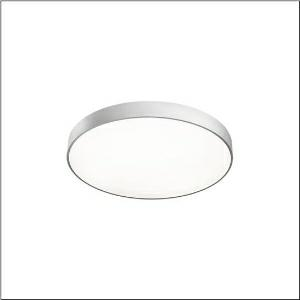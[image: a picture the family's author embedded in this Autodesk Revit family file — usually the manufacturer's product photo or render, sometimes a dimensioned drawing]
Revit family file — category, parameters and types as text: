
# Revit family: round_21_m_51mr36fm8321s
name_source: partatom
category: Lighting Fixtures
units: mm (PartAtom-declared; Revit-internal decimal feet)

## family parameters
Cut with Voids When Loaded = No
Host = Face
Light Source = No
Part Type = Normal
Room Calculation Point = No
Round Connector Dimension = Use Diameter
Shared = No

## types (1)
- --- (1 x LED, 8540 lm, 62.6 W, 3000K)
    Apparent Load = 63 VA
    CIE Flux Codes = 49 80 96 100 100
    Color Rendering = 80
    Color Temperature = 3000K
    Default Elevation = 1800 mm
    Description = Round 21 M, wall and ceiling luminaire, primary optical cover: cover, of PMMA, opal, light emission: direct distribution, primary light characteristic: symmetric, installation type: suspended mounting, surface-mounted, LED, rated luminous flux: 7.700lm, luminous efficacy: 127lm/W, light colour: 830, colour temperature: 3000K, control gear: ON/OFF Multilumen, with terminal, 3-pole, mains connection: 230V, AC, 50/60Hz, rated input power: 61W, housing, of aluminium, coated, silver, diameter: 600mm, height: 62mm, protection rating (complete): IP40, insulation class (complete): insulation class I (protective earthing), certification: CE, impact resistance: IK04, permissible operating ambient temperature: -10..+35°C, packaging unit: 1 piece
    Height = 87 mm
    Lamp = 1 x LED
    Lamp Light Flux = 8540 lm
    Lamp Power = 62.6 W
    Lamp count = 1
    Length = 600 mm
    Luminous efficacy = 136 lm/W
    Manufacturer = Siteco
    ModVariant = No
    Model = 51MR36FM8321S
    Mounting Place = Ceiling
    Mounting Type = Surface mounted
    Number of Poles = 1
    OnlyDefault = Yes
    Power Factor = 1
    Product Name = Round 21 M
    Product group = wall and ceiling luminaire
    ProductGroupID = 304
    Protection Class = Protection class I
    Protection Degree = IP 40
    RLX_Detail_Level = 1
    RLX_Emergency_Light_Flux = 0 lm
    RLX_Emergency_Type = 0
    RLX_Emergency_Type_DB = No
    RlxData = <blob elided: 17473 chars, md5=b82f56c6>
    Socket = socket
    Standby Power = 0 W
    System Light Flux = 8540 lm
    System Power = 63 W
    Type Comments = factory setting: luminous flux: 100 % | (ON | ON | ON | ON) | 700 mA
    Type Image = l_1258303.jpg
    URL = http://relux.com
    VarID = @adj_032782
    Voltage = 0 V
    Weight = 0.00 kg
    Width = 0 mm  [stored 0 ft]

note: [stored X ft] marks values corroborated as IEEE doubles in the binary element streams (Revit-internal decimal feet)

## geometry (parser evidence)
native form markers: Blend x4, Sweep x11
no freeform markers — native parametric forms only
